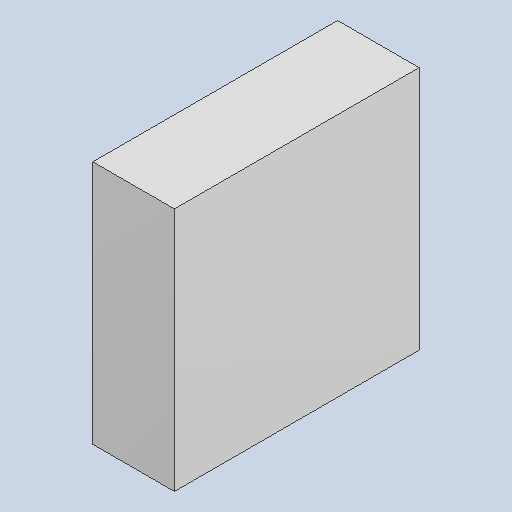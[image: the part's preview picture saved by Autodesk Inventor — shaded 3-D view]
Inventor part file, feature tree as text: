
AUTODESK INVENTOR PART (.ipt)
format: ipt  version: 2023.4 (Build 274418000, 418)  size: 81,408 bytes
history: native  units: mm
features: extrude x1
ambient origin geometry x8: Origin, YZ Plane, XZ Plane, XY Plane, X Axis, Y Axis, Z Axis, Center Point
bodies: Solid1 (feature_tree)
feature tree (1):
  extrude  "Extruded_42"  [1 undecoded]
note: 1 required parameter value undecoded (feature->parameter linkage not recoverable at this tier; creation-order binding heuristic only, values carry confidence <= 0.55)
